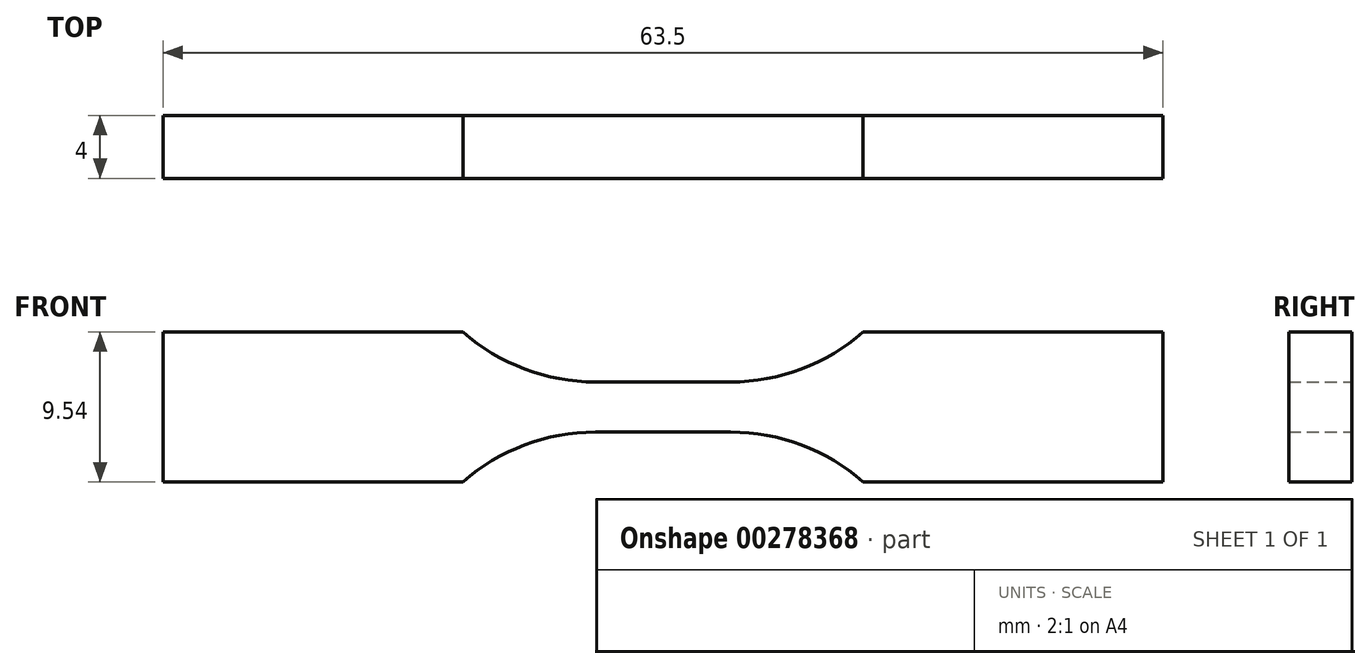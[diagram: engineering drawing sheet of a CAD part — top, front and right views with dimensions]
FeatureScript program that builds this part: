
annotation { "Feature Type Name" : "Feature", "Feature Type Description" : "" }
export const myFeature = defineFeature(function(context is Context, id is Id, definition is map)
    precondition{}
    {
        {
            var Q0;
            Q0=qCreatedBy(makeId("Front.planeOp"),FACE);
            var sketch = newSketch(context, id + "F0", { "sketchPlane" : qUnion([Q0])});
            skLineSegment(sketch, "E0", {"start": v(0, 1.6) * mm, "end": v(4.3, 1.6) * mm});
            skArc(sketch, "E1", {"start": v(4.3, 1.59) * mm, "mid": v(8.79, 2.41) * mm, "end": v(12.7, 4.77) * mm});
            skLineSegment(sketch, "E2", {"start": v(12.7, 4.77) * mm, "end": v(31.75, 4.77) * mm});
            skLineSegment(sketch, "E3.MirrorCS", {"start": v(12.7, -4.77) * mm, "end": v(31.75, -4.77) * mm});
            skLineSegment(sketch, "E4.MirrorCS", {"start": v(0, -1.59) * mm, "end": v(4.3, -1.59) * mm});
            skArc(sketch, "E5.MirrorCS", {"start": v(4.3, -1.59) * mm, "mid": v(8.79, -2.41) * mm, "end": v(12.7, -4.77) * mm});
            skArc(sketch, "E6.MirrorCS", {"start": v(-4.3, -1.59) * mm, "mid": v(-8.79, -2.41) * mm, "end": v(-12.7, -4.77) * mm});
            skLineSegment(sketch, "E7.MirrorCS", {"start": v(0, 1.6) * mm, "end": v(-4.3, 1.6) * mm});
            skArc(sketch, "E8.MirrorCS", {"start": v(-4.3, 1.6) * mm, "mid": v(-8.79, 2.41) * mm, "end": v(-12.7, 4.77) * mm});
            skLineSegment(sketch, "E9.MirrorCS", {"start": v(-12.7, -4.77) * mm, "end": v(-31.75, -4.77) * mm});
            skLineSegment(sketch, "E10.MirrorCS", {"start": v(0, -1.59) * mm, "end": v(-4.3, -1.6) * mm});
            skLineSegment(sketch, "E11.MirrorCS", {"start": v(-12.7, 4.77) * mm, "end": v(-31.75, 4.77) * mm});
            skLineSegment(sketch, "E12", {"start": v(-31.75, -4.76) * mm, "end": v(-31.75, 4.76) * mm});
            skLineSegment(sketch, "E13", {"start": v(31.75, -4.76) * mm, "end": v(31.75, 4.76) * mm});
            skSolve(sketch);
        }
        {
            var Q0;
            Q0 = qSketchRegion(id + "F0", true);
            extrude(context, id + "F1", {"entities" : qUnion([Q0]), "endBound" : BoundingType.SYMMETRIC, "depth" : 4 * mm});
        }
    });
